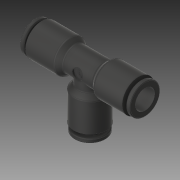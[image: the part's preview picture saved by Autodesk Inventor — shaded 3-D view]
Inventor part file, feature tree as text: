
AUTODESK INVENTOR PART (.ipt)
format: ipt  version: 2018 (Build 220112000, 112)  size: 259,584 bytes
history: native  units: in
note: dims shown in document units (in); Inventor stores cm internally (conversion verified against a paired STEP export)
features: extrude x2, sketch x2
ambient origin geometry x8: Origin, YZ Plane, XZ Plane, XY Plane, X Axis, Y Axis, Z Axis, Center Point
bodies: Solid1 (feature_tree)
feature tree (4):
  extrude  "Extrusion1"  Depth=1.0in TaperAngle=0.0deg
  extrude  "Extrusion2"  Depth=0.578in TaperAngle=0.0deg
  sketch  "Sketch1"  dims[d0=0.25in d1=1.0in d2=0.0in]
  sketch  "Sketch2"  dims[d3=0.25in d4=0.578in d5=0.0in]
